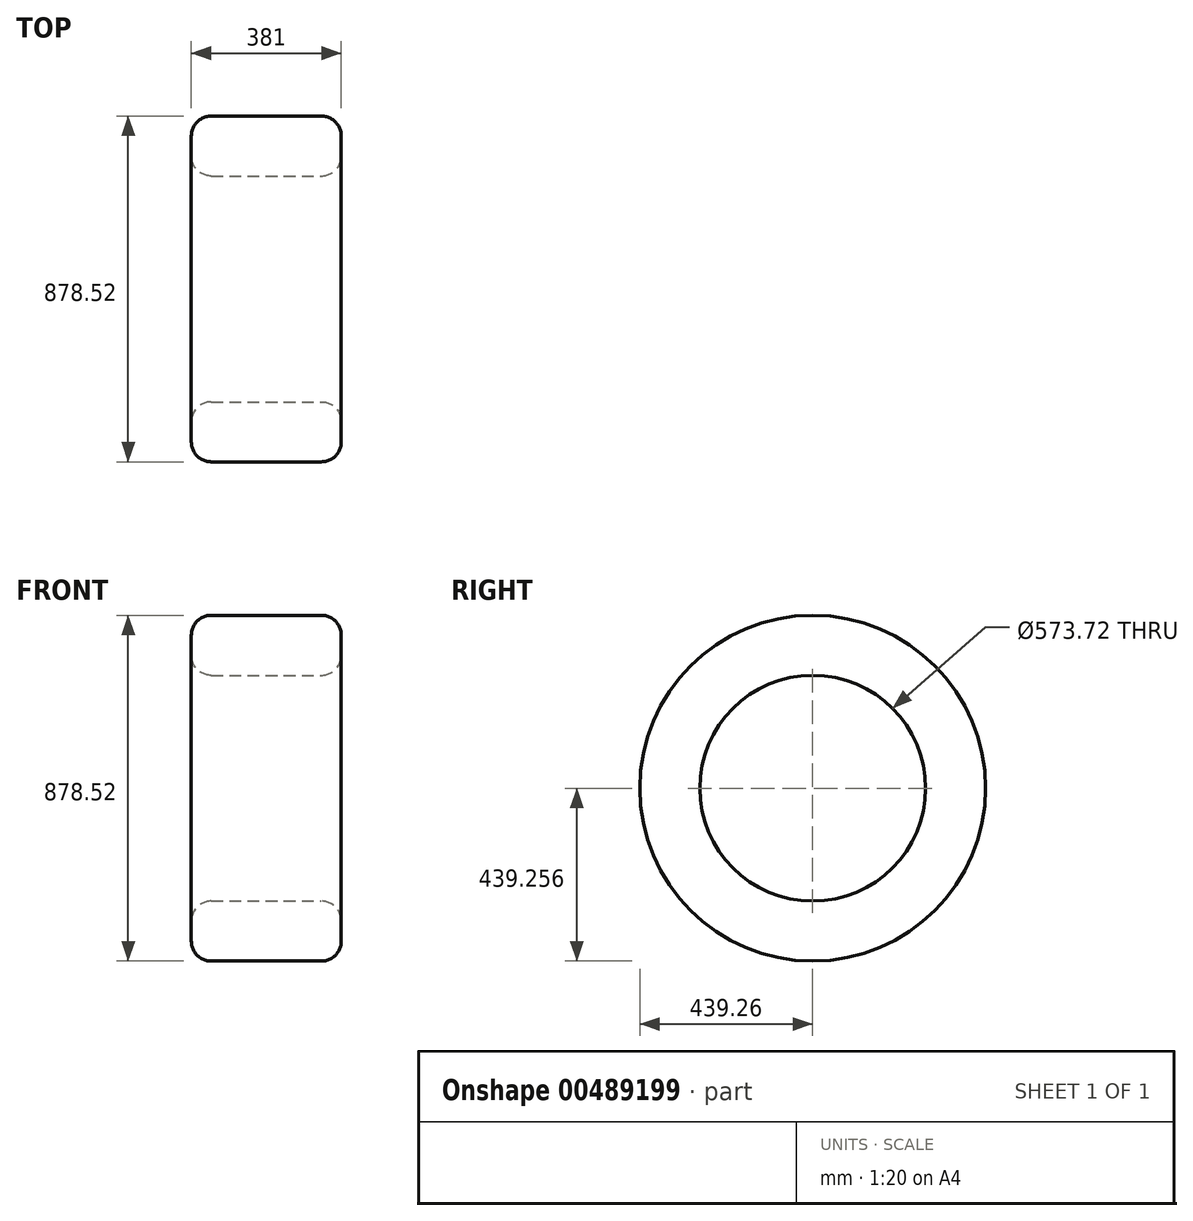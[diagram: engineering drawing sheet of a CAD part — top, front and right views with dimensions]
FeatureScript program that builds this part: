
annotation { "Feature Type Name" : "Feature", "Feature Type Description" : "" }
export const myFeature = defineFeature(function(context is Context, id is Id, definition is map)
    precondition{}
    {
        {
            var Q0;
            Q0=qCreatedBy(makeId("Front.planeOp"),FACE);
            var sketch = newSketch(context, id + "F0", { "sketchPlane" : qUnion([Q0])});
            skLineSegment(sketch, "E0.bottom", {"start": v(-141.65, -100.06) * mm, "end": v(137.75, -100.06) * mm});
            skLineSegment(sketch, "E0.top", {"start": v(-141.65, 52.34) * mm, "end": v(137.75, 52.34) * mm});
            skLineSegment(sketch, "E0.left", {"start": v(-192.45, -49.26) * mm, "end": v(-192.45, 1.54) * mm});
            skLineSegment(sketch, "E0.right", {"start": v(188.55, -49.26) * mm, "end": v(188.55, 1.54) * mm});
            skPoint(sketch, "E1.visualSharp", {"position": v(188.55, 52.34) * mm});
            skArc(sketch, "E1.filletArc", {"start": v(188.55, 1.54) * mm, "mid": v(173.68, 37.46) * mm, "end": v(137.75, 52.34) * mm});
            skPoint(sketch, "E2.visualSharp", {"position": v(188.55, -100.06) * mm});
            skArc(sketch, "E2.filletArc", {"start": v(137.75, -100.06) * mm, "mid": v(173.68, -85.19) * mm, "end": v(188.55, -49.26) * mm});
            skPoint(sketch, "E3.visualSharp", {"position": v(-192.45, -100.06) * mm});
            skArc(sketch, "E3.filletArc", {"start": v(-192.45, -49.26) * mm, "mid": v(-177.57, -85.19) * mm, "end": v(-141.65, -100.06) * mm});
            skPoint(sketch, "E4.visualSharp", {"position": v(-192.45, 52.34) * mm});
            skArc(sketch, "E4.filletArc", {"start": v(-141.65, 52.34) * mm, "mid": v(-177.57, 37.46) * mm, "end": v(-192.45, 1.54) * mm});
            skSolve(sketch);
        }
        {
            var Q0;
            Q0=makeQuery(id+"F0.imprint","IMPRINT",FACE,{"disambiguationData":[TD([[makeQuery(id+"F0.imprint","IMPRINT",EDGE,{"derivedFrom":sQuery(id+"F0.wireOp",EDGE,"E0.bottom")}),1.0]])]});
            var sketch = newSketch(context, id + "F1", { "sketchPlane" : qUnion([Q0])});
            skLineSegment(sketch, "E5", {"start": v(-136.48, -151.28) * mm, "end": v(-272.27, -151.28) * mm});
            skLineSegment(sketch, "E6", {"start": v(-272.27, -151.28) * mm, "end": v(-141.4, -151.28) * mm});
            skLineSegment(sketch, "E7", {"start": v(-141.4, -151.28) * mm, "end": v(-141.4, -151.28) * mm});
            skLineSegment(sketch, "E8", {"start": v(86.34, -151.28) * mm, "end": v(294.89, -151.28) * mm});
            skLineSegment(sketch, "E9", {"start": v(294.89, -151.28) * mm, "end": v(137.52, -151.28) * mm});
            skLineSegment(sketch, "E10", {"start": v(137.52, -151.28) * mm, "end": v(181.19, -75.64) * mm});
            skLineSegment(sketch, "E11", {"start": v(-185.08, -75.64) * mm, "end": v(-228.75, 0) * mm});
            skLineSegment(sketch, "E12", {"start": v(-141.4, -151.28) * mm, "end": v(-185.08, -75.64) * mm});
            skLineSegment(sketch, "E13", {"start": v(137.52, -151.28) * mm, "end": v(137.52, -151.28) * mm});
            skLineSegment(sketch, "E14", {"start": v(181.19, -75.64) * mm, "end": v(224.86, 0) * mm});
            skLineSegment(sketch, "E15", {"start": v(137.52, -151.28) * mm, "end": v(199.78, -151.28) * mm});
            skLineSegment(sketch, "E16", {"start": v(-141.4, -151.28) * mm, "end": v(137.52, -151.28) * mm});
            skSolve(sketch);
        }
        {
            var Q0;
            Q0=makeQuery(id+"F0.imprint","IMPRINT",FACE,{"disambiguationData":[TD([[makeQuery(id+"F0.imprint","IMPRINT",EDGE,{"derivedFrom":sQuery(id+"F0.wireOp",EDGE,"E0.bottom")}),1.0]])]});
            var sketch = newSketch(context, id + "F2", { "sketchPlane" : qUnion([Q0])});
            skLineSegment(sketch, "E17", {"start": v(255.98, -386.92) * mm, "end": v(-278.05, -386.92) * mm});
            skSolve(sketch);
        }
        {
            var Q0;
            Q0=sQuery(id+"F1.wireOp",EDGE,"E16");
            var Q1;
            Q1=sQuery(id+"F1.wireOp",EDGE,"E12");
            var Q2;
            Q2=sQuery(id+"F1.wireOp",EDGE,"E10");
            var Q3;
            Q3=sQuery(id+"F2.wireOp",EDGE,"E17");
            revolve(context, id + "F3", {"bodyType" : ToolBodyType.SURFACE, "surfaceEntities" : qUnion([Q0, Q1, Q2]), "axis" : qUnion([Q3]), "revolveType" : RevolveType.FULL});
        }
        {
            var Q0;
            Q0=makeQuery(id+"F0.imprint","IMPRINT",FACE,{"disambiguationData":[TD([[makeQuery(id+"F0.imprint","IMPRINT",EDGE,{"derivedFrom":sQuery(id+"F0.wireOp",EDGE,"E0.bottom")}),1.0]])]});
            var Q1;
            Q1=sQuery(id+"F2.wireOp",EDGE,"E17");
            revolve(context, id + "F4", {"entities" : qUnion([Q0]), "axis" : qUnion([Q1]), "revolveType" : RevolveType.FULL});
        }
    });
